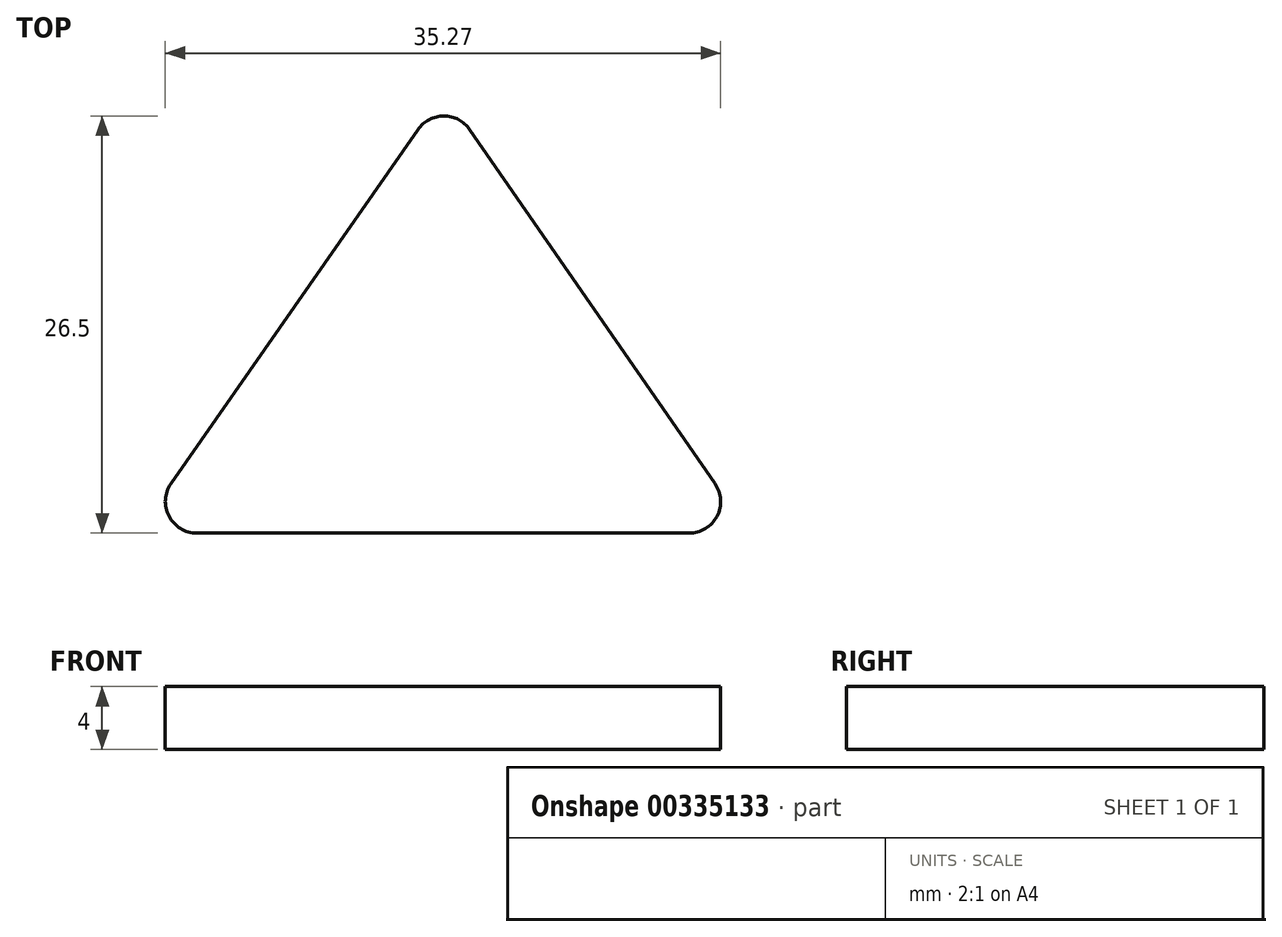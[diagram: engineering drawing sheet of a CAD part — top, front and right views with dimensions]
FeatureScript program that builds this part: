
annotation { "Feature Type Name" : "Feature", "Feature Type Description" : "" }
export const myFeature = defineFeature(function(context is Context, id is Id, definition is map)
    precondition{}
    {
        {
            var Q0;
            Q0=qCreatedBy(makeId("Top.planeOp"),FACE);
            var sketch = newSketch(context, id + "F0", { "sketchPlane" : qUnion([Q0])});
            skLineSegment(sketch, "E0", {"start": v(0, 0) * mm, "end": v(-38.92, 0) * mm});
            skLineSegment(sketch, "E1", {"start": v(-38.92, 0) * mm, "end": v(-19.39, 28) * mm});
            skLineSegment(sketch, "E2", {"start": v(-19.39, 28) * mm, "end": v(0, 0) * mm});
            skSolve(sketch);
        }
        {
            var Q0;
            Q0=makeQuery(id+"F0.imprint","IMPRINT",FACE,{"disambiguationData":[TD([[makeQuery(id+"F0.imprint","IMPRINT",EDGE,{"derivedFrom":sQuery(id+"F0.wireOp",EDGE,"E0")}),-1.0]])]});
            extrude(context, id + "F1", {"entities" : qUnion([Q0]), "depth" : 4 * mm});
        }
        {
            var Q0;
            Q0=makeQuery(id+"F1.opExtrude","SWEPT_EDGE",EDGE,{"disambiguationData":[OSD([sQuery(id+"F0.wireOp",EDGE,"E1"),sQuery(id+"F0.wireOp",EDGE,"E2")])]});
            var Q1;
            Q1=makeQuery(id+"F1.opExtrude","SWEPT_EDGE",EDGE,{"disambiguationData":[OSD([sQuery(id+"F0.wireOp",EDGE,"E0"),sQuery(id+"F0.wireOp",EDGE,"E1")])]});
            var Q2;
            Q2=makeQuery(id+"F1.opExtrude","SWEPT_EDGE",EDGE,{"disambiguationData":[OSD([sQuery(id+"F0.wireOp",EDGE,"E0"),sQuery(id+"F0.wireOp",EDGE,"E2")])]});
            fillet(context, id + "F2", {"entities" : qUnion([Q0, Q1, Q2]), "radius" : 2 * mm, "tangentPropagation" : true, "allowEdgeOverflow" : false});
        }
    });
